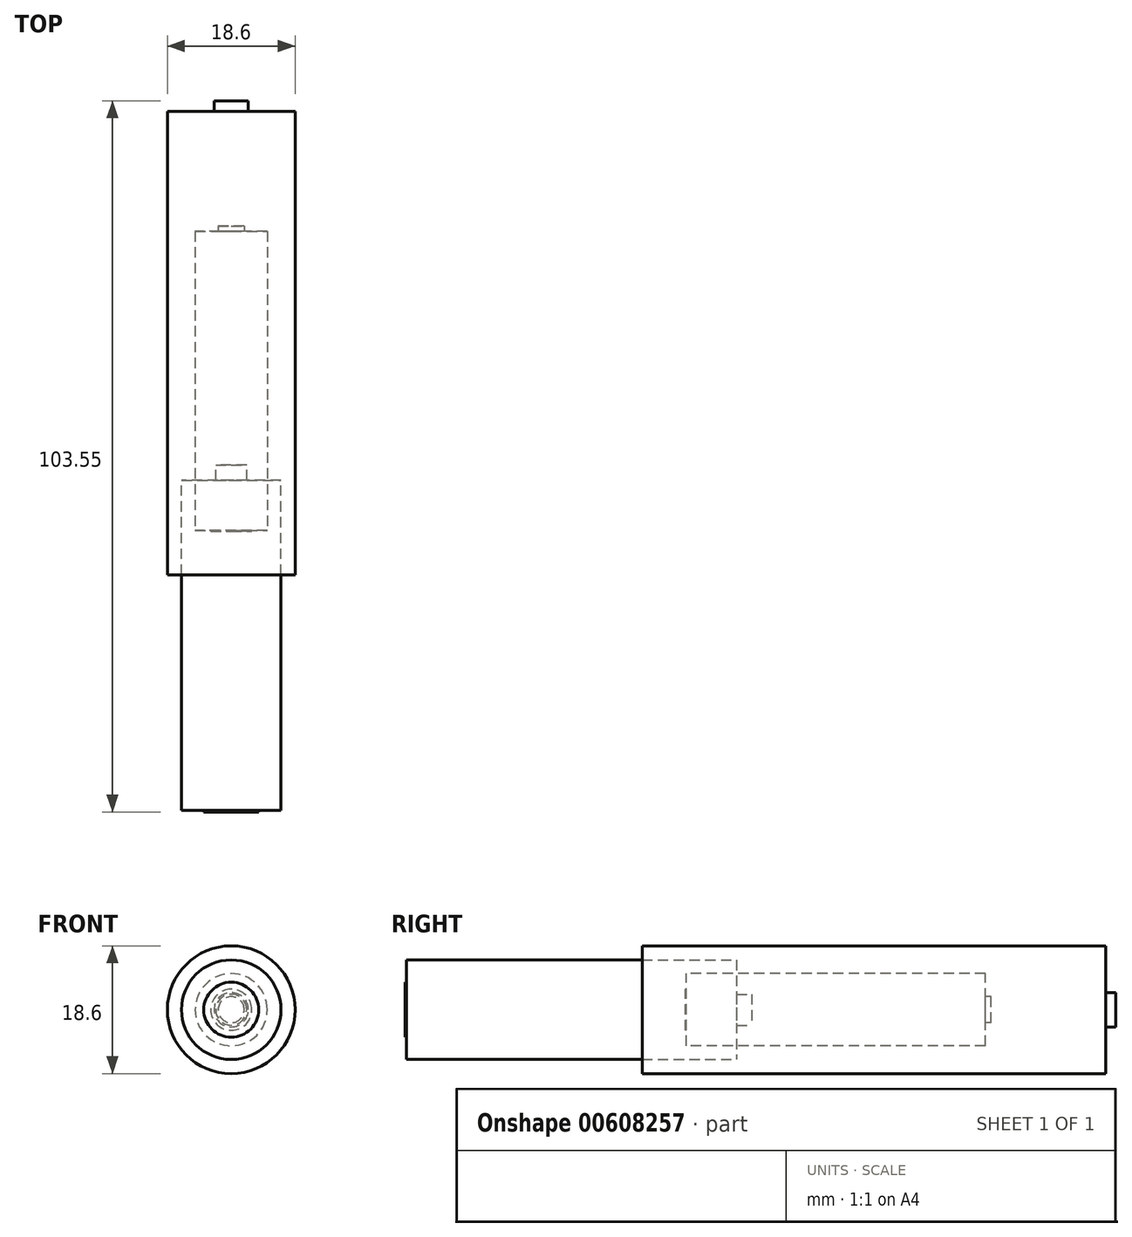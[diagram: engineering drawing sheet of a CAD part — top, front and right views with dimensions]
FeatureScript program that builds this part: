
annotation { "Feature Type Name" : "Feature", "Feature Type Description" : "" }
export const myFeature = defineFeature(function(context is Context, id is Id, definition is map)
    precondition{}
    {
        {
            var Q0;
            Q0=qCreatedBy(makeId("Top.planeOp"),FACE);
            var sketch = newSketch(context, id + "F0", { "sketchPlane" : qUnion([Q0])});
            skLineSegment(sketch, "E0", {"start": v(0, 47.95) * mm, "end": v(0, -12.14) * mm, "construction": true});
            skLineSegment(sketch, "E1", {"start": v(0, 0) * mm, "end": v(2.25, 0) * mm});
            skLineSegment(sketch, "E2", {"start": v(2.25, 0) * mm, "end": v(2.25, -2.2) * mm});
            skLineSegment(sketch, "E3", {"start": v(2.25, -2.2) * mm, "end": v(7.25, -2.2) * mm});
            skLineSegment(sketch, "E4", {"start": v(7.25, -2.2) * mm, "end": v(7.25, -50.3) * mm});
            skLineSegment(sketch, "E5", {"start": v(7.25, -50.3) * mm, "end": v(4, -50.3) * mm});
            skLineSegment(sketch, "E6", {"start": v(4, -50.3) * mm, "end": v(4, -50.5) * mm});
            skLineSegment(sketch, "E7", {"start": v(4, -50.5) * mm, "end": v(0, -50.5) * mm});
            skLineSegment(sketch, "E8", {"start": v(0, -50.5) * mm, "end": v(0, 0) * mm});
            skSolve(sketch);
        }
        {
            var Q0;
            Q0=qSketchRegion(id+"F0",true);
            var Q1;
            Q1=sQuery(id+"F0.wireOp",EDGE,"E0");
            revolve(context, id + "F1", {"entities" : qUnion([Q0]), "axis" : qUnion([Q1]), "revolveType" : RevolveType.FULL});
        }
        {
            var Q0;
            Q0=qCreatedBy(makeId("Top.planeOp"),FACE);
            var sketch = newSketch(context, id + "F2", { "sketchPlane" : qUnion([Q0])});
            skLineSegment(sketch, "E9", {"start": v(0, 34.85) * mm, "end": v(1.9, 34.85) * mm});
            skLineSegment(sketch, "E10", {"start": v(1.9, 34.85) * mm, "end": v(1.9, 34.05) * mm});
            skLineSegment(sketch, "E11", {"start": v(1.9, 34.05) * mm, "end": v(5.25, 34.05) * mm});
            skLineSegment(sketch, "E12", {"start": v(5.25, 34.05) * mm, "end": v(5.25, -9.5) * mm});
            skLineSegment(sketch, "E13", {"start": v(0, -9.65) * mm, "end": v(0, 34.85) * mm});
            skLineSegment(sketch, "E14", {"start": v(0, -9.65) * mm, "end": v(3, -9.65) * mm});
            skLineSegment(sketch, "E15", {"start": v(3, -9.65) * mm, "end": v(3, -9.5) * mm});
            skLineSegment(sketch, "E16", {"start": v(3, -9.5) * mm, "end": v(5.25, -9.5) * mm});
            skSolve(sketch);
        }
        {
            var Q0;
            Q0=qSketchRegion(id+"F2",true);
            var Q1;
            Q1=sQuery(id+"F2.wireOp",EDGE,"E13");
            revolve(context, id + "F3", {"entities" : qUnion([Q0]), "axis" : qUnion([Q1]), "revolveType" : RevolveType.FULL});
        }
        {
            var Q0;
            Q0=qCreatedBy(makeId("Top.planeOp"),FACE);
            var sketch = newSketch(context, id + "F4", { "sketchPlane" : qUnion([Q0])});
            skLineSegment(sketch, "E17", {"start": v(0, 53.05) * mm, "end": v(2.5, 53.05) * mm});
            skLineSegment(sketch, "E18", {"start": v(2.5, 53.05) * mm, "end": v(2.5, 51.55) * mm});
            skLineSegment(sketch, "E19", {"start": v(2.5, 51.55) * mm, "end": v(9.3, 51.55) * mm});
            skLineSegment(sketch, "E20", {"start": v(9.3, 51.55) * mm, "end": v(9.3, -15.95) * mm});
            skLineSegment(sketch, "E21", {"start": v(9.3, -15.95) * mm, "end": v(0, -15.95) * mm});
            skLineSegment(sketch, "E22", {"start": v(0, -15.95) * mm, "end": v(0, 53.05) * mm});
            skSolve(sketch);
        }
        {
            var Q0;
            Q0=qSketchRegion(id+"F4",true);
            var Q1;
            Q1=sQuery(id+"F4.wireOp",EDGE,"E22");
            revolve(context, id + "F5", {"entities" : qUnion([Q0]), "axis" : qUnion([Q1]), "revolveType" : RevolveType.FULL});
        }
    });
